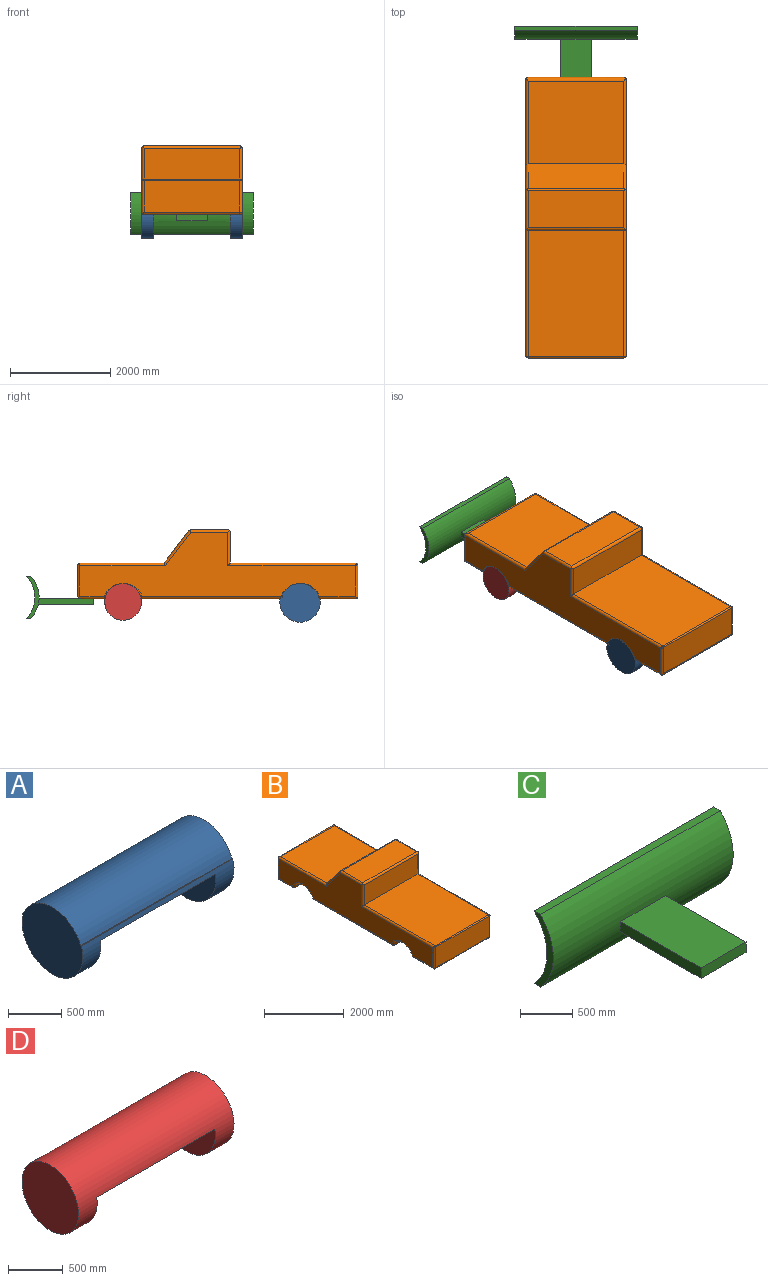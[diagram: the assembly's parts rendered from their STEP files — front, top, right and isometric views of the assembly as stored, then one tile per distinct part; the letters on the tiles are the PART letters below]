
ASSEMBLY  parts=4 mates=3
PART A: 9 faces, bbox 2006.6x805.2x770.9 mm
  f0: cylinder r=402.59mm len=2006.6mm, axis (1,0,0), area 881126.3mm2, adj f1,f2,f4,f5,f6,f7,f8
  f1: plane 2006.6x9.28mm, normal (0,0,1), area 18622.7mm2, adj f0,f3,f4,f5
  f2: plane 2006.6x9.28mm, normal (0,0,1), area 18622.7mm2, adj f0,f3,f4,f5
  f3: cylinder r=406.4mm len=2006.6mm, axis (1,0,0), area 1934975.5mm2, adj f1,f2,f4,f5
  f4: plane 805.18x770.89mm, normal (-1,0,0), area 483904.2mm2, adj f0,f1,f2,f3
  f5: plane 805.18x770.89mm, normal (1,0,0), area 483904.2mm2, adj f0,f1,f2,f3
  f6: plane 805.18x466.09mm, normal (1,0,0), area 305508.8mm2, adj f0,f8
  f7: plane 805.18x466.09mm, normal (-1,0,0), area 305508.8mm2, adj f0,f8
  f8: plane 1524x795.1mm, normal (0,0,-1), area 1211734.1mm2, adj f0,f6,f7
PART B: 47 faces, bbox 2006.6x5588x1371.6 mm
  f0: plane 2849.05x1905mm, normal (0,0,-1), area 5427433.5mm2, adj f1,f11,f23,f40
  f1: cylinder r=355.6mm len=1905mm, axis (-1,0,0), area 1735605.4mm2, adj f0,f2,f21,f39
  f2: plane 1905x497.42mm, normal (0,0,-1), area 947591.3mm2, adj f1,f19,f38,f43
  f3: plane 1905x558.8mm, normal (0,1,0), area 1064514mm2, adj f17,f37,f43,f44
  f4: plane 1905x1651mm, normal (0,0,1), area 3145155mm2, adj f5,f15,f36,f44
  f5: plane 1905x640.57mm, normal (0,0.79,0.61), area 1539560mm2, adj f4,f16,f35,f45
  f6: plane 1905x736.99mm, normal (0,0,1), area 1403958.3mm2, adj f18,f34,f45,f46
  f7: plane 1905x609.6mm, normal (0,-1,0), area 1161288mm2, adj f8,f20,f33,f46
  f8: plane 2514.6x1905mm, normal (0,0,1), area 4790313mm2, adj f7,f14,f22,f32
  f9: plane 1905x635mm, normal (0,-1,0), area 1209675mm2, adj f14,f26,f29,f30
  f10: plane 1905x751.42mm, normal (0,0,-1), area 1431461.3mm2, adj f11,f27,f29,f42
  f11: cylinder r=355.6mm len=1905mm, axis (-1,0,0), area 1735605.4mm2, adj f0,f10,f25,f41
  f12: plane 5486.4x1270mm, normal (1,0,0), area 3721894mm2, adj f15,f16,f17,f18,f19,f20,f21,f22
  f13: plane 5486.4x1270mm, normal (-1,0,0), area 3721894mm2, adj f30,f32,f33,f34,f35,f36,f37,f38
  f14: cylinder r=25.4mm len=1905mm, axis (-1,0,0), area 76006.1mm2, adj f8,f9,f24,f31
  f15: cylinder r=50.8mm len=1729.9mm, axis (0,1,0), area 135099mm2, adj f4,f12,f16,f17,f44
  f16: cylinder r=50.8mm len=709.16mm, axis (0,0.61,-0.79), area 66189.1mm2, adj f5,f12,f15,f18,f45
  f17: cylinder r=50.8mm len=666.56mm, axis (0,0,-1), area 49849.8mm2, adj f3,f12,f15,f19,f43,f44
  f18: cylinder r=50.8mm len=795.35mm, axis (0,1,0), area 61295.4mm2, adj f6,f12,f16,f20,f45,f46
  f19: cylinder r=50.8mm len=551.3mm, axis (0,-1,0), area 41259.7mm2, adj f2,f12,f17,f21,f43
  f20: cylinder r=50.8mm len=696.32mm, axis (0,0,1), area 51628.6mm2, adj f7,f12,f18,f22,f46
  f21: torus R=406.4mm, axis (1,0,0), area 74257.5mm2, adj f1,f12,f19,f23
  f22: cylinder r=50.8mm len=2565.4mm, axis (0,1,0), area 201392.7mm2, adj f8,f12,f20,f24
  f23: cylinder r=50.8mm len=2849.05mm, axis (0,-1,0), area 225218.5mm2, adj f0,f12,f21,f25
  f24: bspline ~60.66x50.8mm, area 2129.2mm2, adj f14,f22,f26
  f25: torus R=406.4mm, axis (1,0,0), area 74257.5mm2, adj f11,f12,f23,f27
  f26: cylinder r=50.8mm len=635mm, axis (0,0,1), area 49934.2mm2, adj f9,f12,f24,f28
  f27: cylinder r=50.8mm len=751.42mm, axis (0,-1,0), area 58898.3mm2, adj f10,f12,f25,f28
  f28: sphere r=50.8mm, area 4053.7mm2, adj f26,f27,f29
  f29: cylinder r=50.8mm len=1940.92mm, axis (-1,0,0), area 153523.9mm2, adj f9,f10,f28,f30,f42
  f30: cylinder r=50.8mm len=670.92mm, axis (0,0,-1), area 51445.9mm2, adj f9,f13,f29,f31,f42
  f31: bspline ~60.66x50.8mm, area 2129.2mm2, adj f14,f30,f32
  f32: cylinder r=50.8mm len=2565.4mm, axis (0,-1,0), area 201392.7mm2, adj f8,f13,f31,f33
  f33: cylinder r=50.8mm len=696.32mm, axis (0,0,-1), area 51628.6mm2, adj f7,f13,f32,f34,f46
  f34: cylinder r=50.8mm len=795.35mm, axis (0,-1,0), area 61295.4mm2, adj f6,f13,f33,f35,f45,f46
  f35: cylinder r=50.8mm len=709.16mm, axis (0,-0.61,0.79), area 66189.1mm2, adj f5,f13,f34,f36,f45
  f36: cylinder r=50.8mm len=1729.9mm, axis (0,-1,0), area 135099mm2, adj f4,f13,f35,f37,f44
  f37: cylinder r=50.8mm len=666.56mm, axis (0,0,1), area 49849.8mm2, adj f3,f13,f36,f38,f43,f44
  f38: cylinder r=50.8mm len=551.3mm, axis (0,1,0), area 41259.7mm2, adj f2,f13,f37,f39,f43
  f39: torus R=406.4mm, axis (1,0,0), area 74257.5mm2, adj f1,f13,f38,f40
  f40: cylinder r=50.8mm len=2849.05mm, axis (0,1,0), area 225218.5mm2, adj f0,f13,f39,f41
  f41: torus R=406.4mm, axis (1,0,0), area 74257.5mm2, adj f11,f13,f40,f42
  f42: cylinder r=50.8mm len=787.34mm, axis (0,1,0), area 60410mm2, adj f10,f13,f29,f30,f41
  f43: cylinder r=76.2mm len=1989.13mm, axis (-1,0,0), area 233458.2mm2, adj f2,f3,f17,f19,f37,f38
  f44: cylinder r=76.2mm len=1989.13mm, axis (-1,0,0), area 233458.2mm2, adj f3,f4,f15,f17,f36,f37
  f45: cylinder r=50.8mm len=1949.88mm, axis (-1,0,0), area 89619.8mm2, adj f5,f6,f16,f18,f34,f35
  f46: cylinder r=50.8mm len=1976.84mm, axis (-1,0,0), area 155035.7mm2, adj f6,f7,f18,f20,f33,f34
PART C: 11 faces, bbox 2438.4x1350.6x851.7 mm
  f0: cylinder r=603.25mm len=2438.4mm, axis (-1,0,0), area 2230369.9mm2, adj f1,f3,f4,f5,f6,f8,f9,f10
  f1: plane 2438.4x86.16mm, normal (0,0,-1), area 210102.3mm2, adj f0,f2,f4,f5
  f2: cylinder r=603.25mm len=2438.4mm, axis (-1,0,0), area 2305698.6mm2, adj f1,f3,f4,f5
  f3: plane 2438.4x85.7mm, normal (0,0,1), area 208962.8mm2, adj f0,f2,f4,f5
  f4: plane 851.71x261.91mm, normal (1,0,0), area 73187.4mm2, adj f0,f1,f2,f3
  f5: plane 851.71x261.91mm, normal (-1,0,0), area 73187.4mm2, adj f0,f1,f2,f3
  f6: plane 1089.25x609.6mm, normal (0,0,1), area 664006.4mm2, adj f0,f7,f9,f10
  f7: plane 609.6x122.04mm, normal (0,-1,0), area 74396.7mm2, adj f6,f8,f9,f10
  f8: plane 1107.2x609.6mm, normal (0,0,-1), area 674951.4mm2, adj f0,f7,f9,f10
  f9: plane 1107.2x122.04mm, normal (1,0,0), area 133769.4mm2, adj f0,f6,f7,f8
  f10: plane 1107.2x122.04mm, normal (-1,0,0), area 133769.4mm2, adj f0,f6,f7,f8
PART D: 6 faces, bbox 2006.6x729.6x729.6 mm
  f0: cylinder r=364.78mm len=2006.6mm, axis (1,0,0), area 2658089.1mm2, adj f1,f2,f3,f4,f5
  f1: plane 729.57x729.57mm, normal (-1,0,0), area 418042.9mm2, adj f0
  f2: plane 729.57x729.57mm, normal (1,0,0), area 418042.9mm2, adj f0
  f3: plane 729.57x428.28mm, normal (1,0,0), area 255114mm2, adj f0,f5
  f4: plane 729.57x428.28mm, normal (-1,0,0), area 255114mm2, adj f0,f5
  f5: plane 1524x718.43mm, normal (0,0,-1), area 1094885.3mm2, adj f0,f3,f4
PLACE A t=(-33.02,-474.56,-584.2)mm
PLACE B t=(-33.02,-485.14,-584.2)mm
PLACE C t=(-1003.3,-86,26.08)mm
PLACE D t=(-33.02,-483.02,-584.2)mm
MATE fastened D.f5 <-> B.f2  axis (0,0,-1) through (970.28,4190.58,-584.2)mm
MATE fastened C.f6 <-> B.f2  axis (0,0,1) through (970.28,4772.66,-584.2)mm
MATE fastened A.f8 <-> B.f0  axis (0,0,-1) through (970.28,668.44,-584.2)mm
